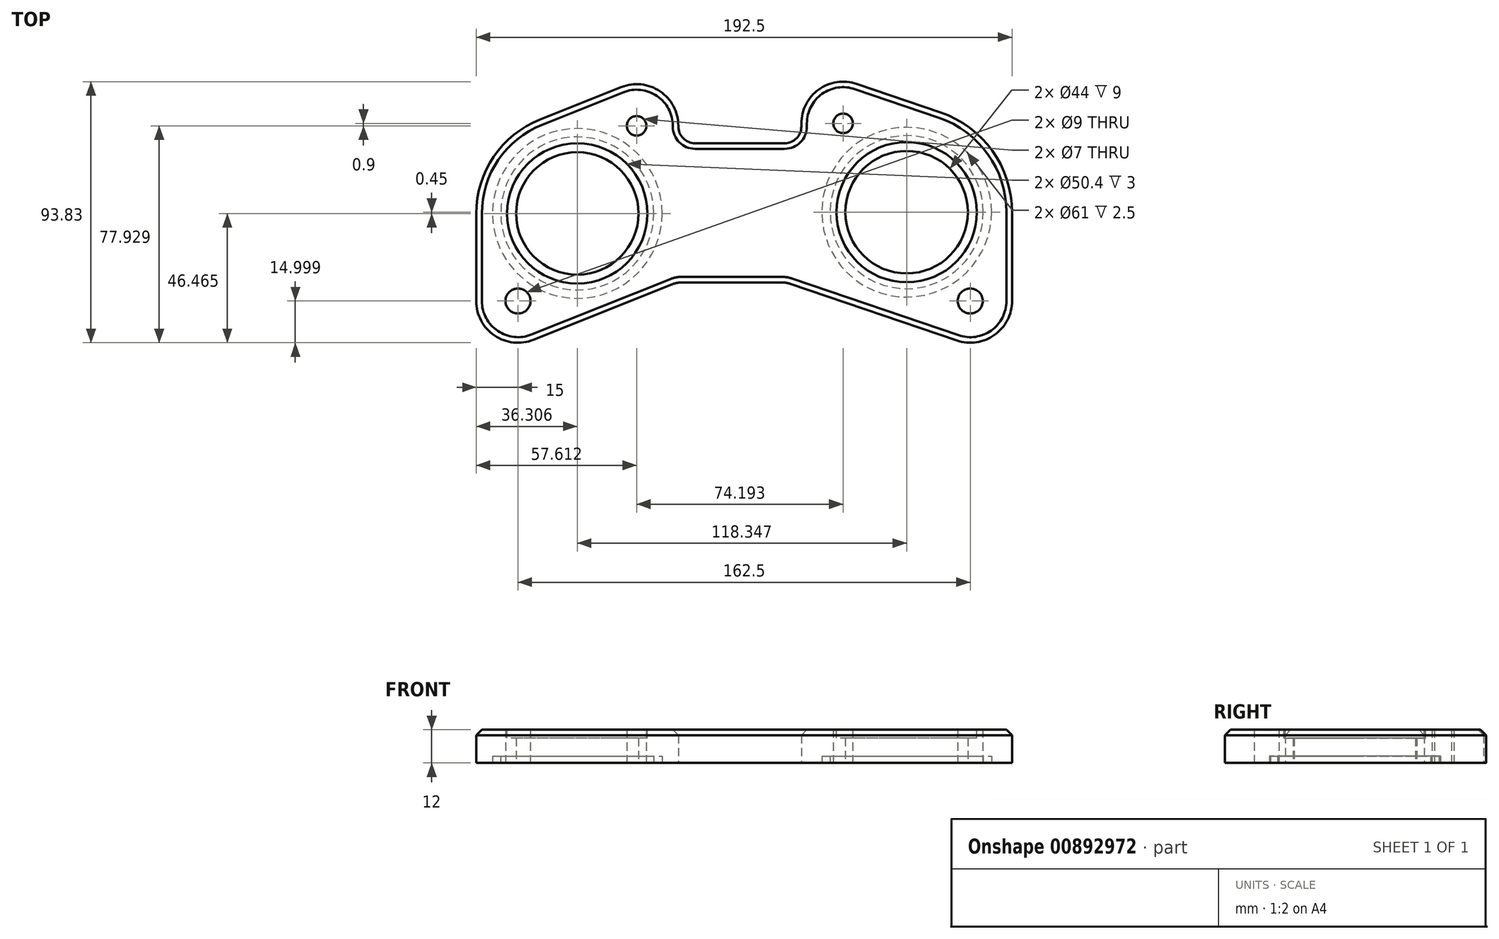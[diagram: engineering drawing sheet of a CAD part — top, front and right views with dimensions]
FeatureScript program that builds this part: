
annotation { "Feature Type Name" : "Feature", "Feature Type Description" : "" }
export const myFeature = defineFeature(function(context is Context, id is Id, definition is map)
    precondition{}
    {
        {
            var Q0;
            Q0=qCreatedBy(makeId("Top.planeOp"),FACE);
            var sketch = newSketch(context, id + "F0", { "sketchPlane" : qUnion([Q0])});
            skCircle(sketch, "E0", {"center": v(81.25, -39.3) * mm, "radius": 4.5 * mm});
            skCircle(sketch, "E1", {"center": v(-81.25, -39.3) * mm, "radius": 4.5 * mm});
            skCircle(sketch, "E2", {"center": v(-38.64, 23.63) * mm, "radius": 3.5 * mm});
            skCircle(sketch, "E3", {"center": v(35.56, 24.53) * mm, "radius": 3.5 * mm});
            skCircle(sketch, "E4", {"center": v(-59.94, -7.84) * mm, "radius": 22 * mm});
            skCircle(sketch, "E5", {"center": v(58.4, -7.39) * mm, "radius": 22 * mm});
            skArc(sketch, "E6", {"start": v(-96.25, -39.3) * mm, "mid": v(-89.66, -51.72) * mm, "end": v(-75.68, -53.23) * mm});
            skArc(sketch, "E7", {"start": v(76.42, -53.5) * mm, "mid": v(89.98, -51.5) * mm, "end": v(96.25, -39.3) * mm});
            skArc(sketch, "E8", {"start": v(40.4, 38.73) * mm, "mid": v(26.82, 36.73) * mm, "end": v(20.56, 24.53) * mm});
            skArc(sketch, "E9", {"start": v(-23.64, 23.63) * mm, "mid": v(-30.23, 36.05) * mm, "end": v(-44.2, 37.56) * mm});
            skArc(sketch, "E10", {"start": v(96.25, -7.39) * mm, "mid": v(89.18, 14.65) * mm, "end": v(70.6, 28.44) * mm});
            skArc(sketch, "E11", {"start": v(-73.42, 25.88) * mm, "mid": v(-90, 12.52) * mm, "end": v(-96.25, -7.84) * mm});
            skLineSegment(sketch, "E12", {"start": v(-44.2, 37.56) * mm, "end": v(-73.42, 25.88) * mm});
            skLineSegment(sketch, "E13", {"start": v(-96.25, -7.84) * mm, "end": v(-96.25, -39.3) * mm});
            skLineSegment(sketch, "E14", {"start": v(70.6, 28.44) * mm, "end": v(40.4, 38.73) * mm});
            skLineSegment(sketch, "E15", {"start": v(96.25, -39.3) * mm, "end": v(96.25, -7.39) * mm});
            skLineSegment(sketch, "E16", {"start": v(-75.68, -53.23) * mm, "end": v(-25.9, -33.33) * mm});
            skArc(sketch, "E17", {"start": v(-25.9, -33.33) * mm, "mid": v(-24.08, -32.8) * mm, "end": v(-22.19, -32.61) * mm});
            skLineSegment(sketch, "E18", {"start": v(-22.19, -32.61) * mm, "end": v(13.41, -32.61) * mm});
            skArc(sketch, "E19", {"start": v(13.41, -32.61) * mm, "mid": v(15.04, -32.74) * mm, "end": v(16.63, -33.14) * mm});
            skLineSegment(sketch, "E20", {"start": v(16.63, -33.14) * mm, "end": v(76.42, -53.5) * mm});
            skLineSegment(sketch, "E21", {"start": v(20.56, 24.53) * mm, "end": v(20.56, 23.39) * mm});
            skArc(sketch, "E22", {"start": v(20.56, 23.39) * mm, "mid": v(18.8, 19.15) * mm, "end": v(14.56, 17.39) * mm});
            skLineSegment(sketch, "E23", {"start": v(14.56, 17.39) * mm, "end": v(-17.64, 17.39) * mm});
            skArc(sketch, "E24", {"start": v(-17.64, 17.39) * mm, "mid": v(-21.88, 19.15) * mm, "end": v(-23.64, 23.39) * mm});
            skLineSegment(sketch, "E25", {"start": v(-23.64, 23.39) * mm, "end": v(-23.64, 23.63) * mm});
            skSolve(sketch);
        }
        {
            var Q0;
            Q0 = qSketchRegion(id + "F0", true);
            extrude(context, id + "F1", {"entities" : qUnion([Q0]), "depth" : 12 * mm, "offsetDistance" : 25 * mm});
        }
        {
            var Q0;
            Q0=makeQuery(id+"F1.opExtrude","CAP_FACE",FACE,{"disambiguationData":[OSD([sQuery(id+"F0.wireOp",EDGE,"E0"),sQuery(id+"F0.wireOp",EDGE,"E1"),sQuery(id+"F0.wireOp",EDGE,"E2"),sQuery(id+"F0.wireOp",EDGE,"E3"),sQuery(id+"F0.wireOp",EDGE,"E4"),sQuery(id+"F0.wireOp",EDGE,"E5"),sQuery(id+"F0.wireOp",EDGE,"E6"),sQuery(id+"F0.wireOp",EDGE,"E7"),sQuery(id+"F0.wireOp",EDGE,"E8"),sQuery(id+"F0.wireOp",EDGE,"E9"),sQuery(id+"F0.wireOp",EDGE,"E10"),sQuery(id+"F0.wireOp",EDGE,"E11"),sQuery(id+"F0.wireOp",EDGE,"E12"),sQuery(id+"F0.wireOp",EDGE,"E13"),sQuery(id+"F0.wireOp",EDGE,"E14"),sQuery(id+"F0.wireOp",EDGE,"E15"),sQuery(id+"F0.wireOp",EDGE,"E16"),sQuery(id+"F0.wireOp",EDGE,"E17"),sQuery(id+"F0.wireOp",EDGE,"E18"),sQuery(id+"F0.wireOp",EDGE,"E19"),sQuery(id+"F0.wireOp",EDGE,"E20"),sQuery(id+"F0.wireOp",EDGE,"E21"),sQuery(id+"F0.wireOp",EDGE,"E22"),sQuery(id+"F0.wireOp",EDGE,"E23"),sQuery(id+"F0.wireOp",EDGE,"E24"),sQuery(id+"F0.wireOp",EDGE,"E25")])],"isStart":false});
            var sketch = newSketch(context, id + "F2", { "sketchPlane" : qUnion([Q0])});
            skCircle(sketch, "E26.0", {"center": v(-59.94, -7.84) * mm, "radius": 25.2 * mm});
            skCircle(sketch, "E27.0", {"center": v(58.4, -7.39) * mm, "radius": 25.2 * mm});
            skSolve(sketch);
        }
        {
            var Q0;
            Q0 = qSketchRegion(id + "F2", true);
            extrude(context, id + "F3", {"entities" : qUnion([Q0]), "operationType" : NewBodyOperationType.REMOVE, "oppositeDirection" : true, "depth" : 3 * mm, "offsetDistance" : 25 * mm});
        }
        {
            var Q0;
            Q0=makeQuery(id+"F1.opExtrude","CAP_EDGE",EDGE,{"disambiguationData":[OSD([sQuery(id+"F0.wireOp",EDGE,"E12")])],"isStart":false});
            chamfer(context, id + "F4", {"entities" : qUnion([Q0]), "width" : 2 * mm, "tangentPropagation" : true});
        }
        {
            var Q0;
            Q0=makeQuery(id+"F1.opExtrude","CAP_FACE",FACE,{"disambiguationData":[OSD([sQuery(id+"F0.wireOp",EDGE,"E0"),sQuery(id+"F0.wireOp",EDGE,"E1"),sQuery(id+"F0.wireOp",EDGE,"E2"),sQuery(id+"F0.wireOp",EDGE,"E3"),sQuery(id+"F0.wireOp",EDGE,"E4"),sQuery(id+"F0.wireOp",EDGE,"E5"),sQuery(id+"F0.wireOp",EDGE,"E6"),sQuery(id+"F0.wireOp",EDGE,"E7"),sQuery(id+"F0.wireOp",EDGE,"E8"),sQuery(id+"F0.wireOp",EDGE,"E9"),sQuery(id+"F0.wireOp",EDGE,"E10"),sQuery(id+"F0.wireOp",EDGE,"E11"),sQuery(id+"F0.wireOp",EDGE,"E12"),sQuery(id+"F0.wireOp",EDGE,"E13"),sQuery(id+"F0.wireOp",EDGE,"E14"),sQuery(id+"F0.wireOp",EDGE,"E15"),sQuery(id+"F0.wireOp",EDGE,"E16"),sQuery(id+"F0.wireOp",EDGE,"E17"),sQuery(id+"F0.wireOp",EDGE,"E18"),sQuery(id+"F0.wireOp",EDGE,"E19"),sQuery(id+"F0.wireOp",EDGE,"E20"),sQuery(id+"F0.wireOp",EDGE,"E21"),sQuery(id+"F0.wireOp",EDGE,"E22"),sQuery(id+"F0.wireOp",EDGE,"E23"),sQuery(id+"F0.wireOp",EDGE,"E24"),sQuery(id+"F0.wireOp",EDGE,"E25")])],"isStart":true});
            var sketch = newSketch(context, id + "F5", { "sketchPlane" : qUnion([Q0])});
            skCircle(sketch, "E28", {"center": v(58.4, 7.39) * mm, "radius": 27.5 * mm});
            skCircle(sketch, "E29", {"center": v(-59.94, 7.84) * mm, "radius": 30.5 * mm});
            skCircle(sketch, "E30", {"center": v(-59.94, 7.84) * mm, "radius": 27.5 * mm});
            skCircle(sketch, "E31", {"center": v(58.4, 7.39) * mm, "radius": 30.5 * mm});
            skSolve(sketch);
        }
        {
            var Q0;
            Q0 = qSketchRegion(id + "F5", true);
            extrude(context, id + "F6", {"entities" : qUnion([Q0]), "operationType" : NewBodyOperationType.REMOVE, "oppositeDirection" : true, "depth" : 2.5 * mm, "offsetDistance" : 25 * mm});
        }
    });
